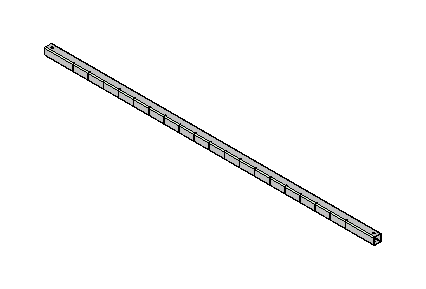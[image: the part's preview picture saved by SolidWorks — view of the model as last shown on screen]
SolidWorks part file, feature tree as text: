
SOLIDWORKS PART (.sldprt)
format: sldprt  version: not decoded by parser v0  size: 405,504 bytes
history: native  units: mm
features: sketch x3, cut_extrude x2, extrude x1, shell x1, pattern_linear x1 (+11 scaffold rows collapsed)
feature tree (19):
  scaffold x11  (default folders/planes/origin — collapsed)
  sketch  "Sketch1"  dims[D3=4.7625mm D1=38.1mm D2=38.1mm]
  extrude  "Extrude1"  Depth=1657.35mm
  shell  "Shell1"  Thickness=2.54mm
  sketch  "Sketch3"  dims[D1=3.175mm D2=76.2mm]
  cut_extrude  "Cut-Extrude2"  Depth=9.525mm
  pattern_linear  "LPattern1"  Count1=10 Count2=10 Spacing1=76.2mm Spacing2=76.2mm
  sketch  "Sketch6"  dims[D1=9.525mm D3=9.525mm D2=19.05mm D4=19.05mm]
  cut_extrude  "Cut-Extrude4"  [1 undecoded]
decode coverage: 7 of 8 modeling features carry decoded parameters
note: 1 parameter value undecoded
note: suppression state not decoded; provenance and decode notes live in map.json
